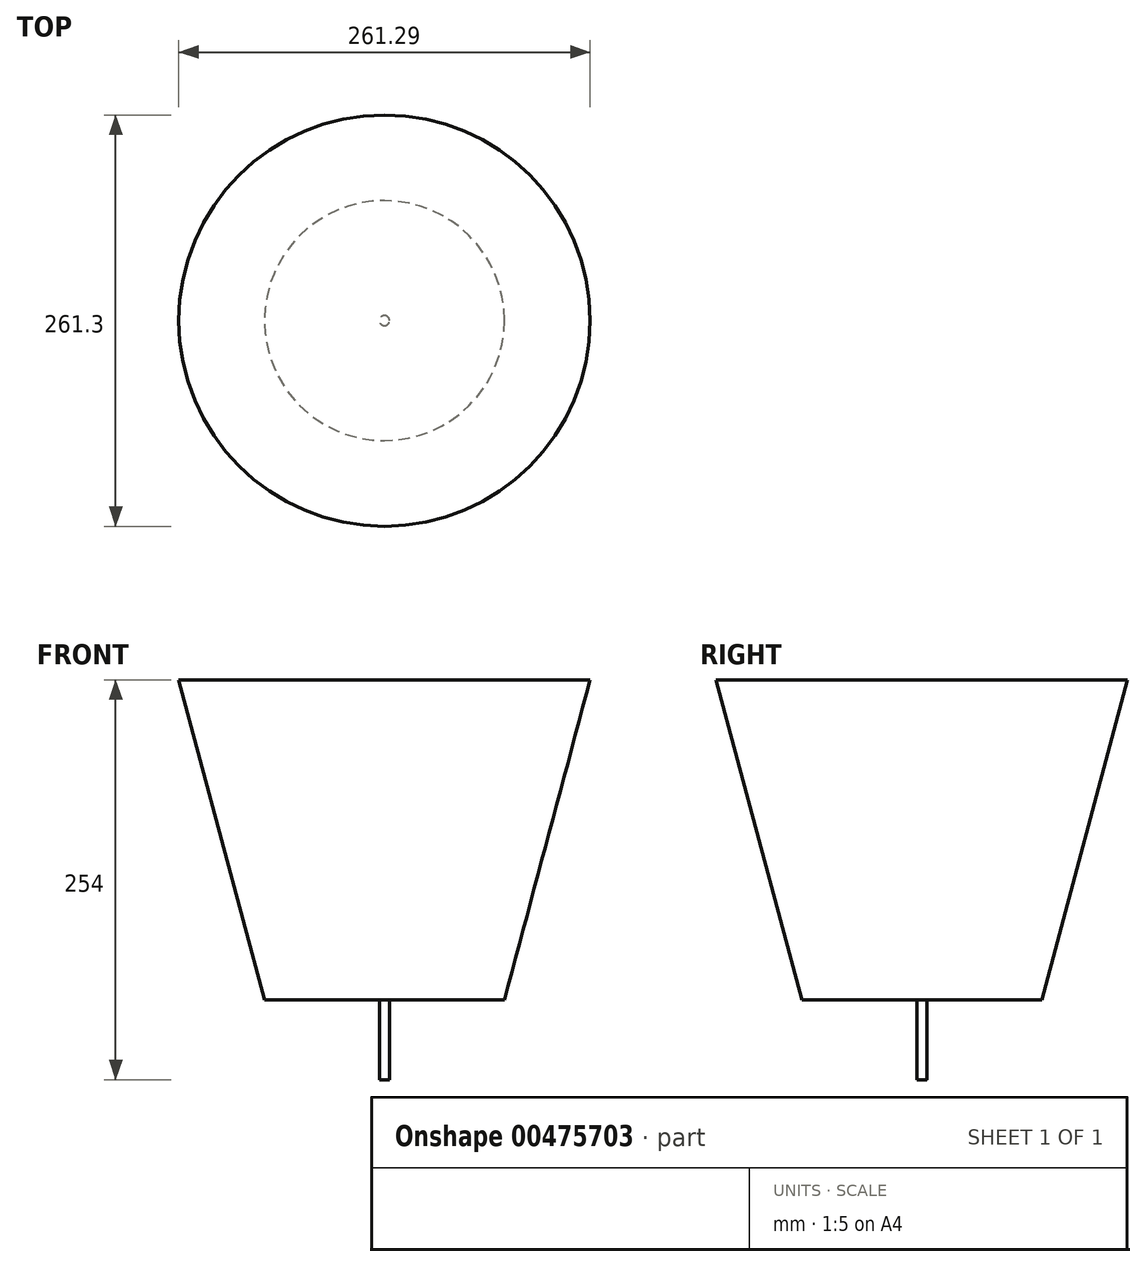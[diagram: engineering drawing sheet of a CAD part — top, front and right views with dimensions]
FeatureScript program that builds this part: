
annotation { "Feature Type Name" : "Feature", "Feature Type Description" : "" }
export const myFeature = defineFeature(function(context is Context, id is Id, definition is map)
    precondition{}
    {
        {
            var Q0;
            Q0=qCreatedBy(makeId("Front.planeOp"),FACE);
            var sketch = newSketch(context, id + "F0", { "sketchPlane" : qUnion([Q0])});
            skLineSegment(sketch, "E0", {"start": v(-3.29, 149.59) * mm, "end": v(-3.29, -53.61) * mm});
            skLineSegment(sketch, "E1", {"start": v(-3.29, -53.61) * mm, "end": v(-79.49, -53.61) * mm});
            skLineSegment(sketch, "E2", {"start": v(-79.49, -53.61) * mm, "end": v(-133.93, 149.59) * mm});
            skLineSegment(sketch, "E3", {"start": v(-133.93, 149.59) * mm, "end": v(-3.29, 149.59) * mm});
            skLineSegment(sketch, "E4", {"start": v(-6.46, -53.61) * mm, "end": v(-6.46, -104.41) * mm});
            skLineSegment(sketch, "E5", {"start": v(-6.46, -104.41) * mm, "end": v(-3.29, -104.41) * mm});
            skLineSegment(sketch, "E6", {"start": v(-3.29, -104.41) * mm, "end": v(-3.29, -53.61) * mm});
            skSolve(sketch);
        }
        {
            var Q0;
            Q0=makeQuery(id+"F0.imprint","IMPRINT",FACE,{"disambiguationData":[TD([[makeQuery(id+"F0.imprint","IMPRINT",EDGE,{"derivedFrom":sQuery(id+"F0.wireOp",EDGE,"E0")}),-1.0]])]});
            var Q1;
            {var subQ2=sQuery(id+"F0.wireOp",EDGE,"E4");Q1=makeQuery(id+"F0.imprint","IMPRINT",FACE,{"disambiguationData":[TD([[makeQuery(id+"F0.imprint","IMPRINT",EDGE,{"derivedFrom":subQ2}),1.0]])]});}
            var Q2;
            Q2=sQuery(id+"F0.wireOp",EDGE,"E0");
            revolve(context, id + "F1", {"entities" : qUnion([Q0, Q1]), "axis" : qUnion([Q2]), "revolveType" : RevolveType.FULL});
        }
    });
